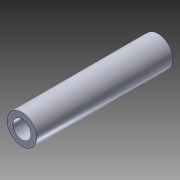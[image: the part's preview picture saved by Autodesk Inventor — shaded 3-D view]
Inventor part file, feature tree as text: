
AUTODESK INVENTOR PART (.ipt)
format: ipt  version: 2013 (Build 170138000, 138)  size: 89,600 bytes
history: native  units: mm
features: extrude x2, sketch x2, plane x1
ambient origin geometry x8: Origin, YZ Plane, XZ Plane, XY Plane, X Axis, Y Axis, Z Axis, Center Point
bodies: Solid1 (feature_tree)
feature tree (5):
  extrude  "Extrusion1"  Depth=3.0mm
  plane  "Work Plane1"
  extrude  "Extrusion2"  Depth=6.0mm
  sketch  "Sketch1"  dims[d0=4.9mm d1=3.0mm]
  sketch  "Sketch2"  dims[d2=22.5mm d3=0.0mm d4=6.0mm d6=4.0mm d7=5.0mm d8=0.5mm d9=0.0mm]
